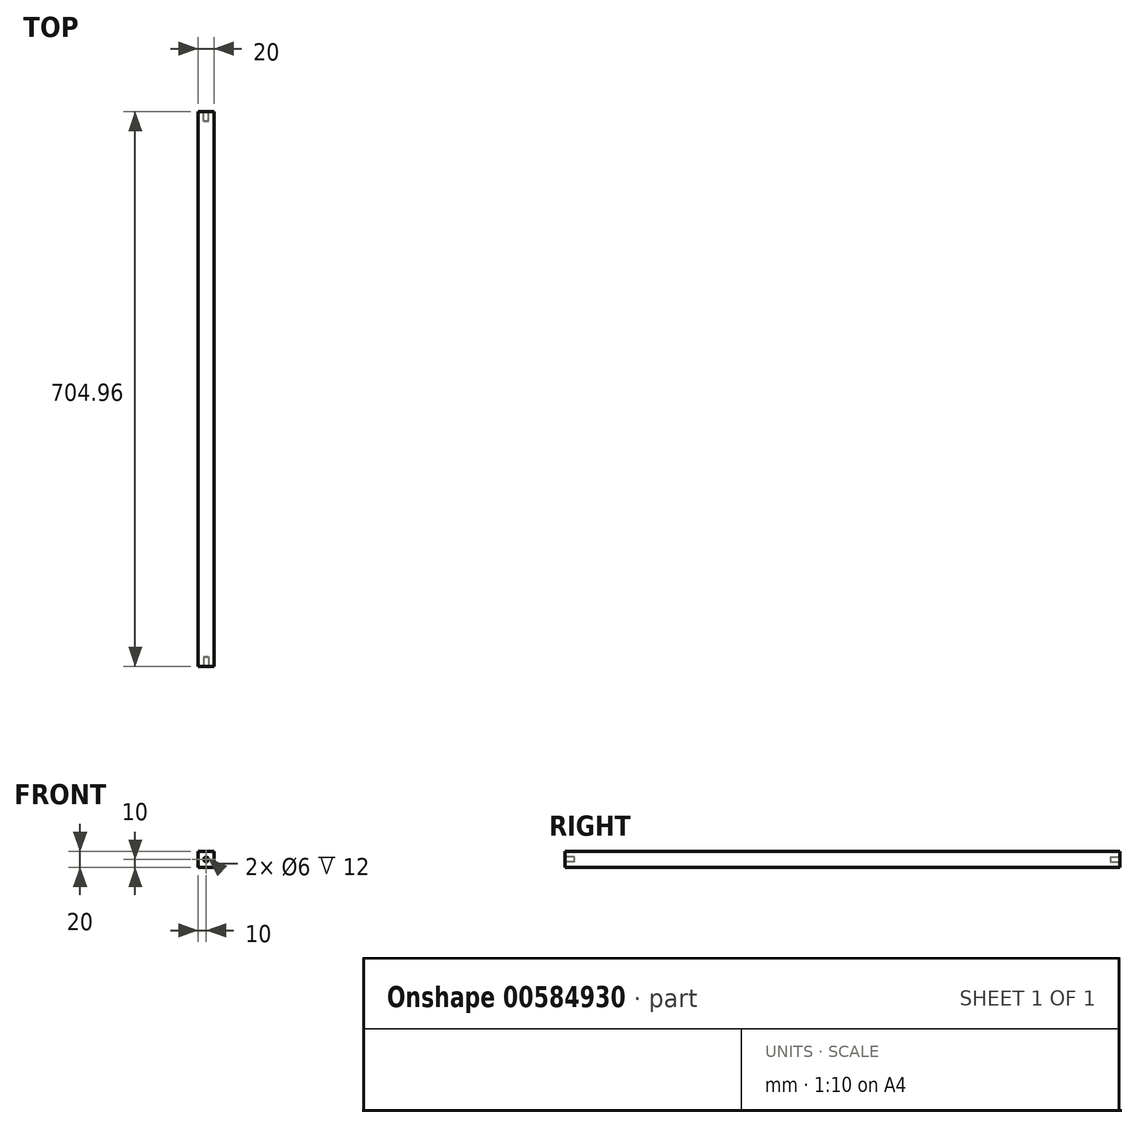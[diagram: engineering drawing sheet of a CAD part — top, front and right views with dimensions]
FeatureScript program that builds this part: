
annotation { "Feature Type Name" : "Feature", "Feature Type Description" : "" }
export const myFeature = defineFeature(function(context is Context, id is Id, definition is map)
    precondition{}
    {
        {
            var Q0;
            Q0=qCreatedBy(makeId("Front.planeOp"),FACE);
            var sketch = newSketch(context, id + "F0", { "sketchPlane" : qUnion([Q0])});
            skLineSegment(sketch, "E0.bottom", {"start": v(0, 0) * mm, "end": v(20, 0) * mm});
            skLineSegment(sketch, "E0.top", {"start": v(0, 20) * mm, "end": v(20, 20) * mm});
            skLineSegment(sketch, "E0.left", {"start": v(0, 0) * mm, "end": v(0, 20) * mm});
            skLineSegment(sketch, "E0.right", {"start": v(20, 0) * mm, "end": v(20, 20) * mm});
            skSolve(sketch);
        }
        {
            var Q0;
            Q0=makeQuery(id+"F0.imprint","IMPRINT",FACE,{"disambiguationData":[TD([[makeQuery(id+"F0.imprint","IMPRINT",EDGE,{"derivedFrom":sQuery(id+"F0.wireOp",EDGE,"E0.bottom")}),1.0]])]});
            extrude(context, id + "F1", {"entities" : qUnion([Q0]), "depth" : 704.97 * mm, "offsetDistance" : 25 * mm, "symmetric" : true});
        }
        {
            var Q0;
            Q0=makeQuery(id+"F1.opExtrude","CAP_FACE",FACE,{"disambiguationData":[OSD([sQuery(id+"F0.wireOp",EDGE,"E0.bottom"),sQuery(id+"F0.wireOp",EDGE,"E0.top"),sQuery(id+"F0.wireOp",EDGE,"E0.left"),sQuery(id+"F0.wireOp",EDGE,"E0.right")])],"isStart":false});
            var sketch = newSketch(context, id + "F2", { "sketchPlane" : qUnion([Q0])});
            skCircle(sketch, "E1", {"center": v(10, 10) * mm, "radius": 3 * mm});
            skSolve(sketch);
        }
        {
            var Q0;
            Q0 = qSketchRegion(id + "F2", true);
            extrude(context, id + "F3", {"entities" : qUnion([Q0]), "operationType" : NewBodyOperationType.REMOVE, "oppositeDirection" : true, "depth" : 12 * mm, "offsetDistance" : 25 * mm});
        }
        {
            var Q0;
            Q0=makeQuery(id+"F1.opExtrude","CAP_FACE",FACE,{"disambiguationData":[OSD([sQuery(id+"F0.wireOp",EDGE,"E0.bottom"),sQuery(id+"F0.wireOp",EDGE,"E0.top"),sQuery(id+"F0.wireOp",EDGE,"E0.left"),sQuery(id+"F0.wireOp",EDGE,"E0.right")])],"isStart":true});
            var sketch = newSketch(context, id + "F4", { "sketchPlane" : qUnion([Q0])});
            skCircle(sketch, "E2", {"center": v(-10, 10) * mm, "radius": 3 * mm});
            skSolve(sketch);
        }
        {
            var Q0;
            Q0=makeQuery(id+"F4.imprint","IMPRINT",FACE,{"disambiguationData":[TD([[makeQuery(id+"F4.imprint","IMPRINT",EDGE,{"derivedFrom":sQuery(id+"F4.wireOp",EDGE,"E2")}),1.0]])]});
            extrude(context, id + "F5", {"entities" : qUnion([Q0]), "operationType" : NewBodyOperationType.REMOVE, "oppositeDirection" : true, "depth" : 12 * mm, "offsetDistance" : 25 * mm});
        }
    });
